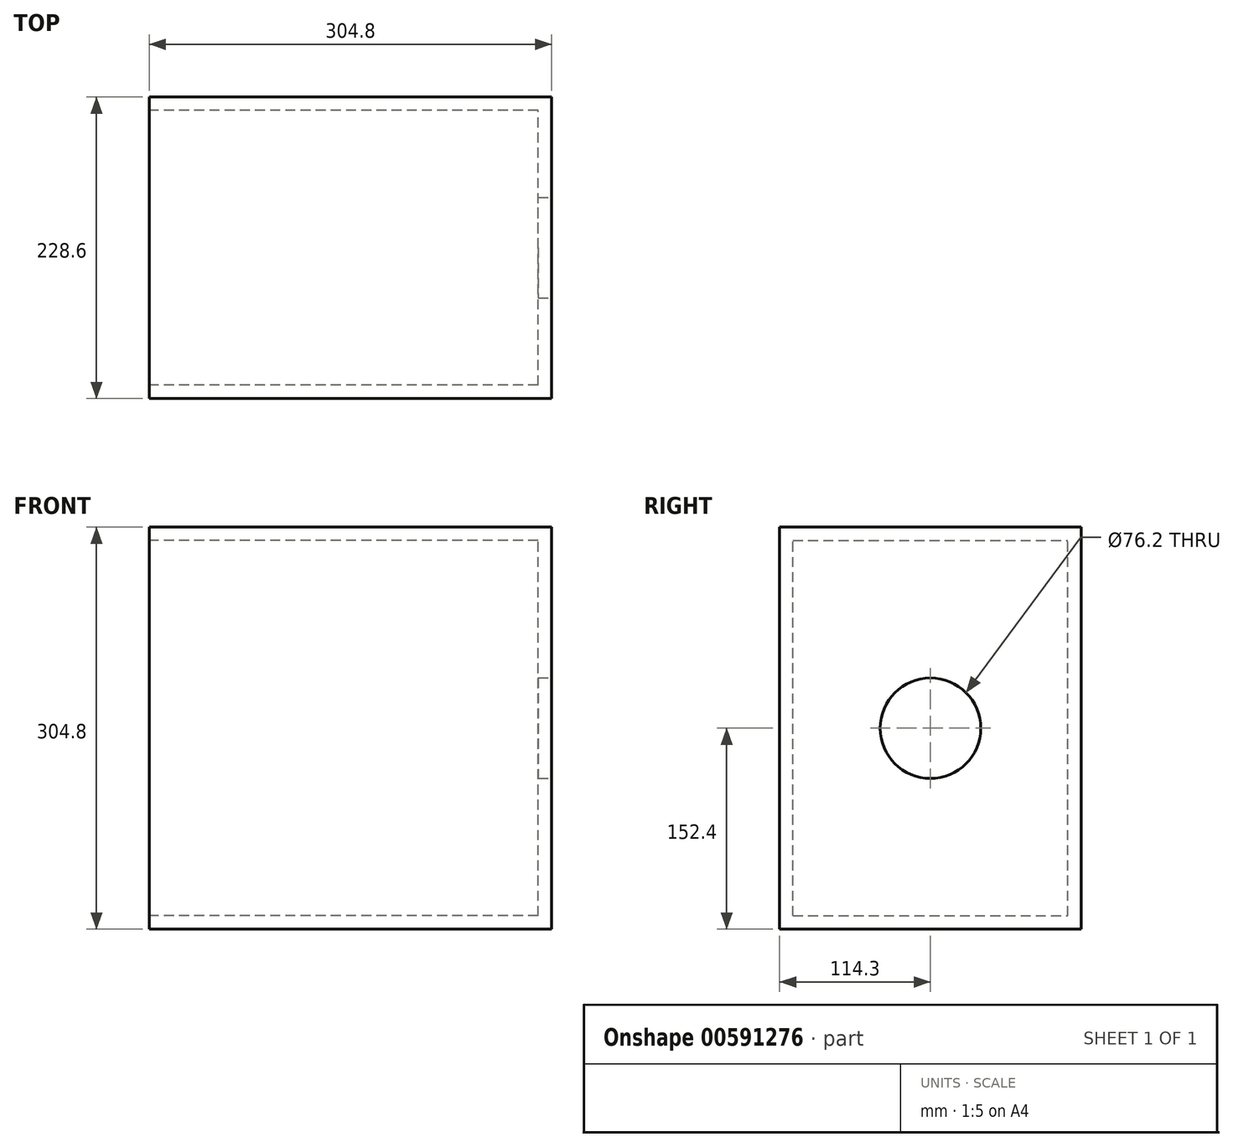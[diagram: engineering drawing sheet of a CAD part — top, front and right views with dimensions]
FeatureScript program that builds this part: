
annotation { "Feature Type Name" : "Feature", "Feature Type Description" : "" }
export const myFeature = defineFeature(function(context is Context, id is Id, definition is map)
    precondition{}
    {
        {
            var Q0;
            Q0=qCreatedBy(makeId("Top.planeOp"),FACE);
            var sketch = newSketch(context, id + "F0", { "sketchPlane" : qUnion([Q0])});
            skLineSegment(sketch, "E0.bottom", {"start": v(-152.4, -114.3) * mm, "end": v(152.4, -114.3) * mm});
            skLineSegment(sketch, "E0.top", {"start": v(-152.4, 114.3) * mm, "end": v(152.4, 114.3) * mm});
            skLineSegment(sketch, "E0.left", {"start": v(-152.4, -114.3) * mm, "end": v(-152.4, 114.3) * mm});
            skLineSegment(sketch, "E0.right", {"start": v(152.4, -114.3) * mm, "end": v(152.4, 114.3) * mm});
            skPoint(sketch, "E0.middle", {"position": v(0, 0) * mm});
            skSolve(sketch);
        }
        {
            var Q0;
            Q0=qSketchRegion(id+"F0",true);
            extrude(context, id + "F1", {"entities" : qUnion([Q0]), "depth" : 304.8 * mm, "offsetDistance" : 25.4 * mm});
        }
        {
            var Q0;
            Q0=makeQuery(id+"F1.opExtrude","SWEPT_FACE",FACE,{"disambiguationData":[OSD([sQuery(id+"F0.wireOp",EDGE,"E0.left")])]});
            var sketch = newSketch(context, id + "F2", { "sketchPlane" : qUnion([Q0])});
            skLineSegment(sketch, "E1.bottom", {"start": v(104.14, 10.16) * mm, "end": v(-104.14, 10.16) * mm});
            skLineSegment(sketch, "E1.top", {"start": v(104.14, 294.64) * mm, "end": v(-104.14, 294.64) * mm});
            skLineSegment(sketch, "E1.left", {"start": v(104.14, 10.16) * mm, "end": v(104.14, 294.64) * mm});
            skLineSegment(sketch, "E1.right", {"start": v(-104.14, 10.16) * mm, "end": v(-104.14, 294.64) * mm});
            skPoint(sketch, "E1.middle", {"position": v(0, 152.4) * mm});
            skPoint(sketch, "E1.middle.positionSnap0", {"position": v(114.3, 152.4) * mm});
            skPoint(sketch, "E1.centerSnap0", {"position": v(114.3, 152.4) * mm});
            skSolve(sketch);
        }
        {
            var Q0;
            Q0=makeQuery(id+"F2.imprint","IMPRINT",FACE,{"disambiguationData":[TD([[makeQuery(id+"F2.imprint","IMPRINT",EDGE,{"derivedFrom":sQuery(id+"F2.wireOp",EDGE,"E1.bottom")}),-1.0]])]});
            extrude(context, id + "F3", {"entities" : qUnion([Q0]), "operationType" : NewBodyOperationType.REMOVE, "oppositeDirection" : true, "depth" : 294.64 * mm, "offsetDistance" : 25.4 * mm});
        }
        {
            var Q0;
            Q0=makeQuery(id+"F1.opExtrude","SWEPT_FACE",FACE,{"disambiguationData":[OSD([sQuery(id+"F0.wireOp",EDGE,"E0.right")])]});
            var sketch = newSketch(context, id + "F4", { "sketchPlane" : qUnion([Q0])});
            skCircle(sketch, "E2", {"center": v(0, 152.4) * mm, "radius": 38.1 * mm});
            skPoint(sketch, "E2.centerSnap0", {"position": v(114.3, 152.4) * mm});
            skSolve(sketch);
        }
        {
            var Q0;
            Q0=makeQuery(id+"F4.imprint","IMPRINT",FACE,{"disambiguationData":[TD([[makeQuery(id+"F4.imprint","IMPRINT",EDGE,{"derivedFrom":sQuery(id+"F4.wireOp",EDGE,"E2")}),1.0]])]});
            extrude(context, id + "F5", {"entities" : qUnion([Q0]), "operationType" : NewBodyOperationType.REMOVE, "oppositeDirection" : true, "depth" : 25.4 * mm, "offsetDistance" : 25.4 * mm});
        }
    });
